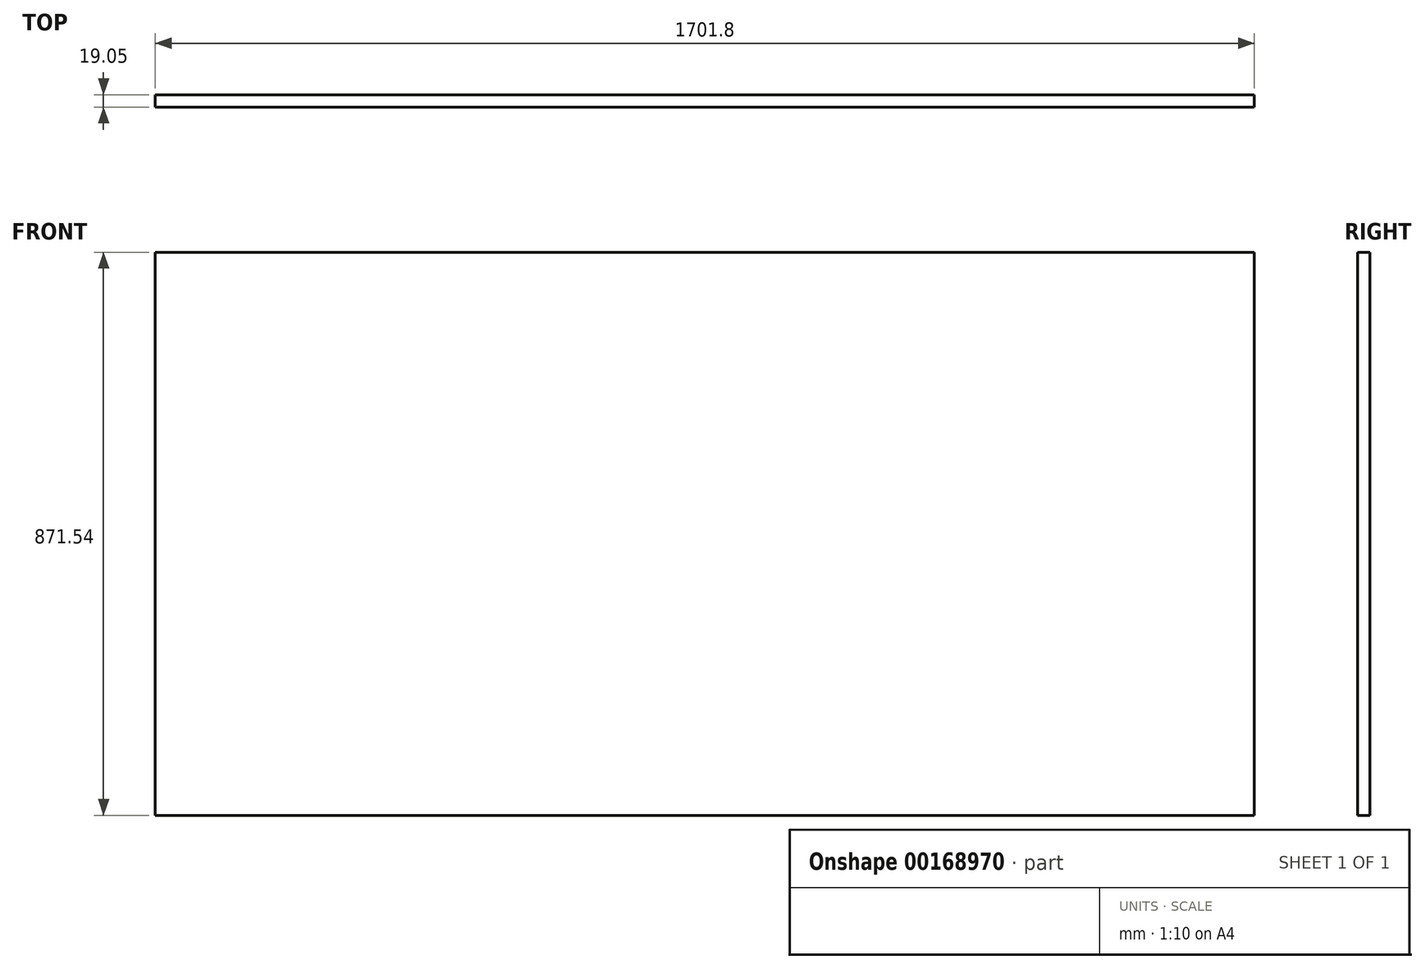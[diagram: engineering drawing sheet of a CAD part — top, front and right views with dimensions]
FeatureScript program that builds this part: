
annotation { "Feature Type Name" : "Feature", "Feature Type Description" : "" }
export const myFeature = defineFeature(function(context is Context, id is Id, definition is map)
    precondition{}
    {
        {
            var Q0;
            Q0=qCreatedBy(makeId("Front.planeOp"),FACE);
            var sketch = newSketch(context, id + "F0", { "sketchPlane" : qUnion([Q0])});
            skLineSegment(sketch, "E0.bottom", {"start": v(-840.7, 398.73) * mm, "end": v(861.1, 398.73) * mm});
            skLineSegment(sketch, "E0.top", {"start": v(-840.7, -472.8) * mm, "end": v(861.1, -472.8) * mm});
            skLineSegment(sketch, "E0.left", {"start": v(-840.7, 398.73) * mm, "end": v(-840.7, -472.8) * mm});
            skLineSegment(sketch, "E0.right", {"start": v(861.1, 398.73) * mm, "end": v(861.1, -472.8) * mm});
            skSolve(sketch);
        }
        {
            var Q0;
            Q0 = qSketchRegion(id + "F0", true);
            extrude(context, id + "F1", {"entities" : qUnion([Q0]), "depth" : 19.05 * mm});
        }
    });
